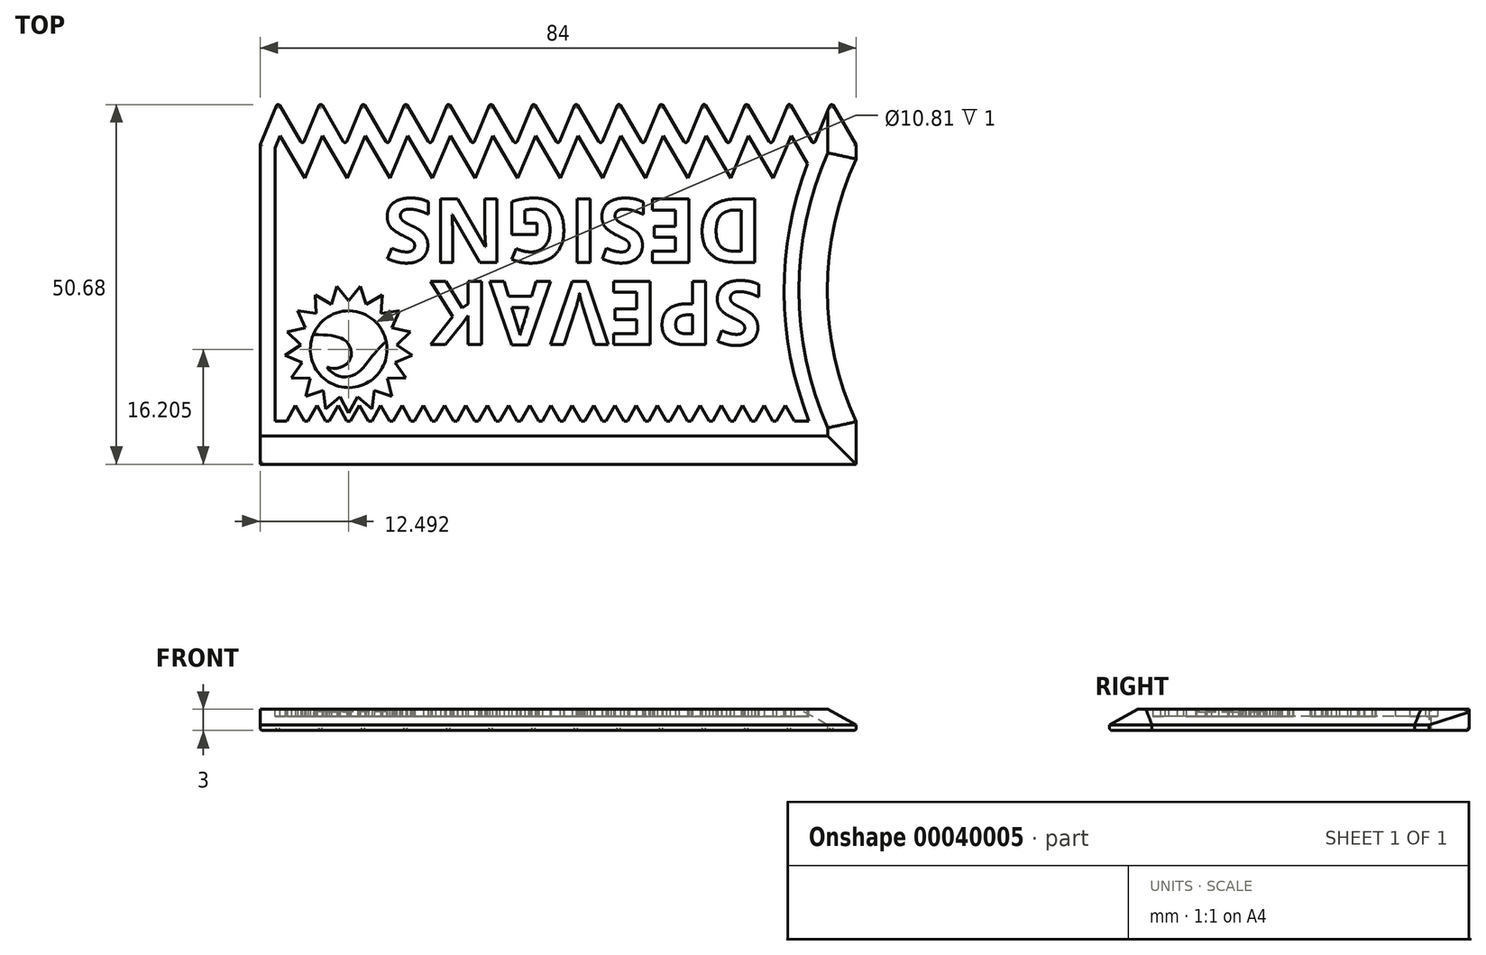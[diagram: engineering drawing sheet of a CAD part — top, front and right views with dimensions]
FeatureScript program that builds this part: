
annotation { "Feature Type Name" : "Feature", "Feature Type Description" : "" }
export const myFeature = defineFeature(function(context is Context, id is Id, definition is map)
    precondition{}
    {
        {
            var Q0;
            Q0=qCreatedBy(makeId("Top.planeOp"),FACE);
            var sketch = newSketch(context, id + "F0", { "sketchPlane" : qUnion([Q0])});
            skLineSegment(sketch, "E0.bottom", {"start": v(0, 0) * mm, "end": v(84, 0) * mm});
            skLineSegment(sketch, "E0.top", {"start": v(2.5, 51) * mm, "end": v(80.5, 51) * mm, "construction": true});
            skLineSegment(sketch, "E0.left", {"start": v(0, 0) * mm, "end": v(0, 45) * mm});
            skLineSegment(sketch, "E0.right", {"start": v(84, 0) * mm, "end": v(84, 45) * mm, "construction": true});
            skLineSegment(sketch, "E1", {"start": v(0, 45) * mm, "end": v(84, 45) * mm, "construction": true});
            skLineSegment(sketch, "E2", {"start": v(0, 45) * mm, "end": v(2.5, 51) * mm});
            skLineSegment(sketch, "E3", {"start": v(2.5, 51) * mm, "end": v(6, 45) * mm});
            skLineSegment(sketch, "E4.1.0.0", {"start": v(6, 45) * mm, "end": v(8.5, 51) * mm});
            skLineSegment(sketch, "E4.1.0.1", {"start": v(8.5, 51) * mm, "end": v(12, 45) * mm});
            skLineSegment(sketch, "E4.2.0.0", {"start": v(12, 45) * mm, "end": v(14.5, 51) * mm});
            skLineSegment(sketch, "E4.2.0.1", {"start": v(14.5, 51) * mm, "end": v(18, 45) * mm});
            skLineSegment(sketch, "E4.3.0.0", {"start": v(18, 45) * mm, "end": v(20.5, 51) * mm});
            skLineSegment(sketch, "E4.3.0.1", {"start": v(20.5, 51) * mm, "end": v(24, 45) * mm});
            skLineSegment(sketch, "E4.4.0.0", {"start": v(24, 45) * mm, "end": v(26.5, 51) * mm});
            skLineSegment(sketch, "E4.4.0.1", {"start": v(26.5, 51) * mm, "end": v(30, 45) * mm});
            skLineSegment(sketch, "E4.5.0.0", {"start": v(30, 45) * mm, "end": v(32.5, 51) * mm});
            skLineSegment(sketch, "E4.5.0.1", {"start": v(32.5, 51) * mm, "end": v(36, 45) * mm});
            skLineSegment(sketch, "E4.6.0.0", {"start": v(36, 45) * mm, "end": v(38.5, 51) * mm});
            skLineSegment(sketch, "E4.6.0.1", {"start": v(38.5, 51) * mm, "end": v(42, 45) * mm});
            skLineSegment(sketch, "E4.7.0.0", {"start": v(42, 45) * mm, "end": v(44.5, 51) * mm});
            skLineSegment(sketch, "E4.7.0.1", {"start": v(44.5, 51) * mm, "end": v(48, 45) * mm});
            skLineSegment(sketch, "E4.8.0.0", {"start": v(48, 45) * mm, "end": v(50.5, 51) * mm});
            skLineSegment(sketch, "E4.8.0.1", {"start": v(50.5, 51) * mm, "end": v(54, 45) * mm});
            skLineSegment(sketch, "E4.9.0.0", {"start": v(54, 45) * mm, "end": v(56.5, 51) * mm});
            skLineSegment(sketch, "E4.9.0.1", {"start": v(56.5, 51) * mm, "end": v(60, 45) * mm});
            skLineSegment(sketch, "E4.10.0.0", {"start": v(60, 45) * mm, "end": v(62.5, 51) * mm});
            skLineSegment(sketch, "E4.10.0.1", {"start": v(62.5, 51) * mm, "end": v(66, 45) * mm});
            skLineSegment(sketch, "E4.11.0.0", {"start": v(66, 45) * mm, "end": v(68.5, 51) * mm});
            skLineSegment(sketch, "E4.11.0.1", {"start": v(68.5, 51) * mm, "end": v(72, 45) * mm});
            skLineSegment(sketch, "E4.12.0.0", {"start": v(72, 45) * mm, "end": v(74.5, 51) * mm});
            skLineSegment(sketch, "E4.12.0.1", {"start": v(74.5, 51) * mm, "end": v(78, 45) * mm});
            skLineSegment(sketch, "E4.13.0.0", {"start": v(78, 45) * mm, "end": v(80.5, 51) * mm});
            skLineSegment(sketch, "E4.13.0.1", {"start": v(80.5, 51) * mm, "end": v(84, 45) * mm});
            skLineSegment(sketch, "E4.direction1", {"start": v(0, 45) * mm, "end": v(6, 45) * mm, "construction": true});
            skLineSegment(sketch, "E5", {"start": v(84, 45) * mm, "end": v(84, 43) * mm});
            skArc(sketch, "E6", {"start": v(84, 43) * mm, "mid": v(79.93, 24.5) * mm, "end": v(84, 6) * mm});
            skLineSegment(sketch, "E7", {"start": v(84, 6) * mm, "end": v(84, 0) * mm});
            skSolve(sketch);
        }
        {
            var Q0;
            Q0=qSketchRegion(id+"F0",true);
            extrude(context, id + "F1", {"entities" : qUnion([Q0]), "depth" : 3 * mm});
        }
        {
            var Q0;
            Q0=makeQuery(id+"F1.opExtrude","CAP_EDGE",EDGE,{"disambiguationData":[OSD([sQuery(id+"F0.wireOp",EDGE,"E5")])],"isStart":false});
            var Q1;
            Q1=makeQuery(id+"F1.opExtrude","CAP_EDGE",EDGE,{"disambiguationData":[OSD([sQuery(id+"F0.wireOp",EDGE,"E6")])],"isStart":false});
            var Q2;
            Q2=makeQuery(id+"F1.opExtrude","CAP_EDGE",EDGE,{"disambiguationData":[OSD([sQuery(id+"F0.wireOp",EDGE,"E0.bottom")])],"isStart":false});
            var Q3;
            Q3=makeQuery(id+"F1.opExtrude","CAP_EDGE",EDGE,{"disambiguationData":[OSD([sQuery(id+"F0.wireOp",EDGE,"E7")])],"isStart":false});
            chamfer(context, id + "F2", {"entities" : qUnion([Q0, Q1, Q2, Q3]), "chamferType" : ChamferType.TWO_OFFSETS, "width1" : 2.2 * mm, "oppositeDirection" : false, "width2" : 4 * mm, "tangentPropagation" : true});
        }
        {
            var Q0;
            Q0=makeQuery(id+"F1.opExtrude","CAP_FACE",FACE,{"disambiguationData":[OSD([sQuery(id+"F0.wireOp",EDGE,"E0.bottom"),sQuery(id+"F0.wireOp",EDGE,"E0.left"),sQuery(id+"F0.wireOp",EDGE,"E2"),sQuery(id+"F0.wireOp",EDGE,"E3"),sQuery(id+"F0.wireOp",EDGE,"E4.1.0.0"),sQuery(id+"F0.wireOp",EDGE,"E4.1.0.1"),sQuery(id+"F0.wireOp",EDGE,"E4.2.0.0"),sQuery(id+"F0.wireOp",EDGE,"E4.2.0.1"),sQuery(id+"F0.wireOp",EDGE,"E4.3.0.0"),sQuery(id+"F0.wireOp",EDGE,"E4.3.0.1"),sQuery(id+"F0.wireOp",EDGE,"E4.4.0.0"),sQuery(id+"F0.wireOp",EDGE,"E4.4.0.1"),sQuery(id+"F0.wireOp",EDGE,"E4.5.0.0"),sQuery(id+"F0.wireOp",EDGE,"E4.5.0.1"),sQuery(id+"F0.wireOp",EDGE,"E4.6.0.0"),sQuery(id+"F0.wireOp",EDGE,"E4.6.0.1"),sQuery(id+"F0.wireOp",EDGE,"E4.7.0.0"),sQuery(id+"F0.wireOp",EDGE,"E4.7.0.1"),sQuery(id+"F0.wireOp",EDGE,"E4.8.0.0"),sQuery(id+"F0.wireOp",EDGE,"E4.8.0.1"),sQuery(id+"F0.wireOp",EDGE,"E4.9.0.0"),sQuery(id+"F0.wireOp",EDGE,"E4.9.0.1"),sQuery(id+"F0.wireOp",EDGE,"E4.10.0.0"),sQuery(id+"F0.wireOp",EDGE,"E4.10.0.1"),sQuery(id+"F0.wireOp",EDGE,"E4.11.0.0"),sQuery(id+"F0.wireOp",EDGE,"E4.11.0.1"),sQuery(id+"F0.wireOp",EDGE,"E4.12.0.0"),sQuery(id+"F0.wireOp",EDGE,"E4.12.0.1"),sQuery(id+"F0.wireOp",EDGE,"E4.13.0.0"),sQuery(id+"F0.wireOp",EDGE,"E4.13.0.1"),sQuery(id+"F0.wireOp",EDGE,"E5"),sQuery(id+"F0.wireOp",EDGE,"E6"),sQuery(id+"F0.wireOp",EDGE,"E7")])],"isStart":false});
            var sketch = newSketch(context, id + "F3", { "sketchPlane" : qUnion([Q0])});
            skLineSegment(sketch, "E8.0", {"start": v(2.1, 44.58) * mm, "end": v(2.1, 6.1) * mm});
            skLineSegment(sketch, "E8.1", {"start": v(2.81, 46.3) * mm, "end": v(2.1, 44.58) * mm});
            skLineSegment(sketch, "E8.2", {"start": v(6.31, 40.3) * mm, "end": v(2.81, 46.3) * mm});
            skLineSegment(sketch, "E8.3", {"start": v(8.81, 46.3) * mm, "end": v(6.31, 40.3) * mm});
            skLineSegment(sketch, "E8.4", {"start": v(12.31, 40.3) * mm, "end": v(8.81, 46.3) * mm});
            skLineSegment(sketch, "E8.5", {"start": v(14.81, 46.3) * mm, "end": v(12.31, 40.3) * mm});
            skLineSegment(sketch, "E8.6", {"start": v(18.31, 40.3) * mm, "end": v(14.81, 46.3) * mm});
            skLineSegment(sketch, "E8.7", {"start": v(2.1, 6.1) * mm, "end": v(77.32, 6.1) * mm});
            skArc(sketch, "E8.8", {"start": v(77.32, 6.1) * mm, "mid": v(73.83, 24.2) * mm, "end": v(77.11, 42.35) * mm});
            skLineSegment(sketch, "E8.9", {"start": v(77.11, 42.35) * mm, "end": v(74.81, 46.3) * mm});
            skLineSegment(sketch, "E8.10", {"start": v(74.81, 46.3) * mm, "end": v(72.31, 40.3) * mm});
            skLineSegment(sketch, "E8.11", {"start": v(72.31, 40.3) * mm, "end": v(68.81, 46.3) * mm});
            skLineSegment(sketch, "E8.12", {"start": v(68.81, 46.3) * mm, "end": v(66.31, 40.3) * mm});
            skLineSegment(sketch, "E8.13", {"start": v(66.31, 40.3) * mm, "end": v(62.81, 46.3) * mm});
            skLineSegment(sketch, "E8.14", {"start": v(62.81, 46.3) * mm, "end": v(60.31, 40.3) * mm});
            skLineSegment(sketch, "E8.15", {"start": v(60.31, 40.3) * mm, "end": v(56.81, 46.3) * mm});
            skLineSegment(sketch, "E8.16", {"start": v(56.81, 46.3) * mm, "end": v(54.31, 40.3) * mm});
            skLineSegment(sketch, "E8.17", {"start": v(54.31, 40.3) * mm, "end": v(50.81, 46.3) * mm});
            skLineSegment(sketch, "E8.18", {"start": v(50.81, 46.3) * mm, "end": v(48.31, 40.3) * mm});
            skLineSegment(sketch, "E8.19", {"start": v(48.31, 40.3) * mm, "end": v(44.81, 46.3) * mm});
            skLineSegment(sketch, "E8.20", {"start": v(44.81, 46.3) * mm, "end": v(42.31, 40.3) * mm});
            skLineSegment(sketch, "E8.21", {"start": v(42.31, 40.3) * mm, "end": v(38.81, 46.3) * mm});
            skLineSegment(sketch, "E8.22", {"start": v(38.81, 46.3) * mm, "end": v(36.31, 40.3) * mm});
            skLineSegment(sketch, "E8.23", {"start": v(36.31, 40.3) * mm, "end": v(32.81, 46.3) * mm});
            skLineSegment(sketch, "E8.24", {"start": v(32.81, 46.3) * mm, "end": v(30.31, 40.3) * mm});
            skLineSegment(sketch, "E8.25", {"start": v(30.31, 40.3) * mm, "end": v(26.81, 46.3) * mm});
            skLineSegment(sketch, "E8.26", {"start": v(26.81, 46.3) * mm, "end": v(24.31, 40.3) * mm});
            skLineSegment(sketch, "E8.27", {"start": v(24.31, 40.3) * mm, "end": v(20.81, 46.3) * mm});
            skLineSegment(sketch, "E8.28", {"start": v(20.81, 46.3) * mm, "end": v(18.31, 40.3) * mm});
            skSolve(sketch);
        }
        {
            var Q0;
            Q0=makeQuery(id+"F3.imprint","IMPRINT",FACE,{"disambiguationData":[TD([[makeQuery(id+"F3.imprint","IMPRINT",EDGE,{"derivedFrom":sQuery(id+"F3.wireOp",EDGE,"E8.0")}),1.0]])]});
            extrude(context, id + "F4", {"entities" : qUnion([Q0]), "operationType" : NewBodyOperationType.REMOVE, "oppositeDirection" : true, "depth" : 1 * mm});
        }
        {
            var Q0;
            Q0=makeQuery(id+"F4.boolean.opBoolean","COPY",FACE,{"derivedFrom":makeQuery(id+"F4.opExtrude","CAP_FACE",FACE,{"disambiguationData":[OSD([sQuery(id+"F3.wireOp",EDGE,"E8.0"),sQuery(id+"F3.wireOp",EDGE,"E8.1"),sQuery(id+"F3.wireOp",EDGE,"E8.2"),sQuery(id+"F3.wireOp",EDGE,"E8.3"),sQuery(id+"F3.wireOp",EDGE,"E8.4"),sQuery(id+"F3.wireOp",EDGE,"E8.5"),sQuery(id+"F3.wireOp",EDGE,"E8.6"),sQuery(id+"F3.wireOp",EDGE,"E8.7"),sQuery(id+"F3.wireOp",EDGE,"E8.8"),sQuery(id+"F3.wireOp",EDGE,"E8.9"),sQuery(id+"F3.wireOp",EDGE,"E8.10"),sQuery(id+"F3.wireOp",EDGE,"E8.11"),sQuery(id+"F3.wireOp",EDGE,"E8.12"),sQuery(id+"F3.wireOp",EDGE,"E8.13"),sQuery(id+"F3.wireOp",EDGE,"E8.14"),sQuery(id+"F3.wireOp",EDGE,"E8.15"),sQuery(id+"F3.wireOp",EDGE,"E8.16"),sQuery(id+"F3.wireOp",EDGE,"E8.17"),sQuery(id+"F3.wireOp",EDGE,"E8.18"),sQuery(id+"F3.wireOp",EDGE,"E8.19"),sQuery(id+"F3.wireOp",EDGE,"E8.20"),sQuery(id+"F3.wireOp",EDGE,"E8.21"),sQuery(id+"F3.wireOp",EDGE,"E8.22"),sQuery(id+"F3.wireOp",EDGE,"E8.23"),sQuery(id+"F3.wireOp",EDGE,"E8.24"),sQuery(id+"F3.wireOp",EDGE,"E8.25"),sQuery(id+"F3.wireOp",EDGE,"E8.26"),sQuery(id+"F3.wireOp",EDGE,"E8.27"),sQuery(id+"F3.wireOp",EDGE,"E8.28")])],"isStart":false})});
            var sketch = newSketch(context, id + "F5", { "sketchPlane" : qUnion([Q0])});
            skLineSegment(sketch, "E9", {"start": v(39.71, 6.1) * mm, "end": v(39.71, 40.3) * mm, "construction": true});
            skText(sketch, "E10", { "text": "SPEVAK", "fontName": "OpenSans-Bold.ttf"});
            skText(sketch, "E11", { "text": "DESIGNS", "fontName": "OpenSans-Bold.ttf"});
            skCircle(sketch, "E12", {"center": v(12.5, 16.2) * mm, "radius": 6.8 * mm, "construction": true});
            skCircle(sketch, "E13", {"center": v(12.5, 16.2) * mm, "radius": 9 * mm, "construction": true});
            skLineSegment(sketch, "E14", {"start": v(12.5, 16.2) * mm, "end": v(12.5, 7.2) * mm, "construction": true});
            skLineSegment(sketch, "E15", {"start": v(13.74, 9.52) * mm, "end": v(12.5, 7.2) * mm});
            skLineSegment(sketch, "E16.MirrorCS", {"start": v(11.24, 9.52) * mm, "end": v(12.5, 7.2) * mm});
            skLineSegment(sketch, "E17", {"start": v(12.5, 16.2) * mm, "end": v(13.74, 9.52) * mm, "construction": true});
            skLineSegment(sketch, "E18.1.0", {"start": v(16.07, 10.42) * mm, "end": v(15.74, 7.81) * mm});
            skLineSegment(sketch, "E18.1.1", {"start": v(13.74, 9.52) * mm, "end": v(15.74, 7.81) * mm});
            skLineSegment(sketch, "E18.2.0", {"start": v(17.92, 12.1) * mm, "end": v(18.56, 9.55) * mm});
            skLineSegment(sketch, "E18.2.1", {"start": v(16.07, 10.42) * mm, "end": v(18.56, 9.55) * mm});
            skLineSegment(sketch, "E18.3.0", {"start": v(19.04, 14.34) * mm, "end": v(20.55, 12.2) * mm});
            skLineSegment(sketch, "E18.3.1", {"start": v(17.92, 12.1) * mm, "end": v(20.55, 12.2) * mm});
            skLineSegment(sketch, "E18.4.0", {"start": v(19.27, 16.83) * mm, "end": v(21.45, 15.37) * mm});
            skLineSegment(sketch, "E18.4.1", {"start": v(19.04, 14.34) * mm, "end": v(21.45, 15.37) * mm});
            skLineSegment(sketch, "E18.5.0", {"start": v(18.58, 19.24) * mm, "end": v(21.15, 18.67) * mm});
            skLineSegment(sketch, "E18.5.1", {"start": v(19.27, 16.83) * mm, "end": v(21.15, 18.67) * mm});
            skLineSegment(sketch, "E18.6.0", {"start": v(17.08, 21.23) * mm, "end": v(19.67, 21.63) * mm});
            skLineSegment(sketch, "E18.6.1", {"start": v(18.58, 19.24) * mm, "end": v(19.67, 21.63) * mm});
            skLineSegment(sketch, "E18.7.0", {"start": v(14.95, 22.55) * mm, "end": v(17.23, 23.86) * mm});
            skLineSegment(sketch, "E18.7.1", {"start": v(17.08, 21.23) * mm, "end": v(17.23, 23.86) * mm});
            skLineSegment(sketch, "E18.8.0", {"start": v(12.5, 23) * mm, "end": v(14.15, 25.05) * mm});
            skLineSegment(sketch, "E18.8.1", {"start": v(14.95, 22.55) * mm, "end": v(14.15, 25.05) * mm});
            skLineSegment(sketch, "E18.9.0", {"start": v(10.03, 22.55) * mm, "end": v(10.84, 25.05) * mm});
            skLineSegment(sketch, "E18.9.1", {"start": v(12.5, 23) * mm, "end": v(10.84, 25.05) * mm});
            skLineSegment(sketch, "E18.10.0", {"start": v(7.9, 21.23) * mm, "end": v(7.75, 23.86) * mm});
            skLineSegment(sketch, "E18.10.1", {"start": v(10.03, 22.55) * mm, "end": v(7.75, 23.86) * mm});
            skLineSegment(sketch, "E18.11.0", {"start": v(6.4, 19.24) * mm, "end": v(5.3, 21.63) * mm});
            skLineSegment(sketch, "E18.11.1", {"start": v(7.9, 21.23) * mm, "end": v(5.3, 21.63) * mm});
            skLineSegment(sketch, "E18.12.0", {"start": v(5.72, 16.83) * mm, "end": v(3.84, 18.67) * mm});
            skLineSegment(sketch, "E18.12.1", {"start": v(6.4, 19.24) * mm, "end": v(3.84, 18.67) * mm});
            skLineSegment(sketch, "E18.13.0", {"start": v(5.95, 14.34) * mm, "end": v(3.53, 15.37) * mm});
            skLineSegment(sketch, "E18.13.1", {"start": v(5.72, 16.83) * mm, "end": v(3.53, 15.37) * mm});
            skLineSegment(sketch, "E18.14.0", {"start": v(7.06, 12.1) * mm, "end": v(4.44, 12.2) * mm});
            skLineSegment(sketch, "E18.14.1", {"start": v(5.95, 14.34) * mm, "end": v(4.44, 12.2) * mm});
            skLineSegment(sketch, "E18.15.0", {"start": v(8.91, 10.42) * mm, "end": v(6.43, 9.55) * mm});
            skLineSegment(sketch, "E18.15.1", {"start": v(7.06, 12.1) * mm, "end": v(6.43, 9.55) * mm});
            skLineSegment(sketch, "E18.16.0", {"start": v(11.24, 9.52) * mm, "end": v(9.24, 7.81) * mm});
            skLineSegment(sketch, "E18.16.1", {"start": v(8.91, 10.42) * mm, "end": v(9.24, 7.81) * mm});
            skCircle(sketch, "E19", {"center": v(12.5, 16.2) * mm, "radius": 5.4 * mm});
            skLineSegment(sketch, "E20", {"start": v(3.75, 6.1) * mm, "end": v(5, 8.3) * mm});
            skLineSegment(sketch, "E21", {"start": v(5, 8.3) * mm, "end": v(6.25, 6.1) * mm});
            skLineSegment(sketch, "E22", {"start": v(6.25, 6.1) * mm, "end": v(3.75, 6.1) * mm, "construction": true});
            skLineSegment(sketch, "E23", {"start": v(5, 6.1) * mm, "end": v(5, 9.23) * mm, "construction": true});
            skLineSegment(sketch, "E24", {"start": v(3.75, 6.1) * mm, "end": v(6.25, 6.1) * mm});
            skLineSegment(sketch, "E25", {"start": v(6.25, 6.1) * mm, "end": v(3.75, 6.1) * mm});
            skLineSegment(sketch, "E26.1.0.0", {"start": v(6.75, 6.1) * mm, "end": v(9.25, 6.1) * mm});
            skLineSegment(sketch, "E26.1.0.1", {"start": v(6.75, 6.1) * mm, "end": v(8, 8.3) * mm});
            skLineSegment(sketch, "E26.1.0.2", {"start": v(8, 8.3) * mm, "end": v(9.25, 6.1) * mm});
            skLineSegment(sketch, "E26.2.0.0", {"start": v(9.75, 6.1) * mm, "end": v(12.25, 6.1) * mm});
            skLineSegment(sketch, "E26.2.0.1", {"start": v(9.75, 6.1) * mm, "end": v(11, 8.3) * mm});
            skLineSegment(sketch, "E26.2.0.2", {"start": v(11, 8.3) * mm, "end": v(12.25, 6.1) * mm});
            skLineSegment(sketch, "E26.3.0.0", {"start": v(12.75, 6.1) * mm, "end": v(15.25, 6.1) * mm});
            skLineSegment(sketch, "E26.3.0.1", {"start": v(12.75, 6.1) * mm, "end": v(14, 8.3) * mm});
            skLineSegment(sketch, "E26.3.0.2", {"start": v(14, 8.3) * mm, "end": v(15.25, 6.1) * mm});
            skLineSegment(sketch, "E26.4.0.0", {"start": v(15.75, 6.1) * mm, "end": v(18.25, 6.1) * mm});
            skLineSegment(sketch, "E26.4.0.1", {"start": v(15.75, 6.1) * mm, "end": v(17, 8.3) * mm});
            skLineSegment(sketch, "E26.4.0.2", {"start": v(17, 8.3) * mm, "end": v(18.25, 6.1) * mm});
            skLineSegment(sketch, "E26.5.0.0", {"start": v(18.75, 6.1) * mm, "end": v(21.25, 6.1) * mm});
            skLineSegment(sketch, "E26.5.0.1", {"start": v(18.75, 6.1) * mm, "end": v(20, 8.3) * mm});
            skLineSegment(sketch, "E26.5.0.2", {"start": v(20, 8.3) * mm, "end": v(21.25, 6.1) * mm});
            skLineSegment(sketch, "E26.6.0.0", {"start": v(21.75, 6.1) * mm, "end": v(24.25, 6.1) * mm});
            skLineSegment(sketch, "E26.6.0.1", {"start": v(21.75, 6.1) * mm, "end": v(23, 8.3) * mm});
            skLineSegment(sketch, "E26.6.0.2", {"start": v(23, 8.3) * mm, "end": v(24.25, 6.1) * mm});
            skLineSegment(sketch, "E26.7.0.0", {"start": v(24.75, 6.1) * mm, "end": v(27.25, 6.1) * mm});
            skLineSegment(sketch, "E26.7.0.1", {"start": v(24.75, 6.1) * mm, "end": v(26, 8.3) * mm});
            skLineSegment(sketch, "E26.7.0.2", {"start": v(26, 8.3) * mm, "end": v(27.25, 6.1) * mm});
            skLineSegment(sketch, "E26.8.0.0", {"start": v(27.75, 6.1) * mm, "end": v(30.25, 6.1) * mm});
            skLineSegment(sketch, "E26.8.0.1", {"start": v(27.75, 6.1) * mm, "end": v(29, 8.3) * mm});
            skLineSegment(sketch, "E26.8.0.2", {"start": v(29, 8.3) * mm, "end": v(30.25, 6.1) * mm});
            skLineSegment(sketch, "E26.9.0.0", {"start": v(30.75, 6.1) * mm, "end": v(33.25, 6.1) * mm});
            skLineSegment(sketch, "E26.9.0.1", {"start": v(30.75, 6.1) * mm, "end": v(32, 8.3) * mm});
            skLineSegment(sketch, "E26.9.0.2", {"start": v(32, 8.3) * mm, "end": v(33.25, 6.1) * mm});
            skLineSegment(sketch, "E26.10.0.0", {"start": v(33.75, 6.1) * mm, "end": v(36.25, 6.1) * mm});
            skLineSegment(sketch, "E26.10.0.1", {"start": v(33.75, 6.1) * mm, "end": v(35, 8.3) * mm});
            skLineSegment(sketch, "E26.10.0.2", {"start": v(35, 8.3) * mm, "end": v(36.25, 6.1) * mm});
            skLineSegment(sketch, "E26.11.0.0", {"start": v(36.75, 6.1) * mm, "end": v(39.25, 6.1) * mm});
            skLineSegment(sketch, "E26.11.0.1", {"start": v(36.75, 6.1) * mm, "end": v(38, 8.3) * mm});
            skLineSegment(sketch, "E26.11.0.2", {"start": v(38, 8.3) * mm, "end": v(39.25, 6.1) * mm});
            skLineSegment(sketch, "E26.12.0.0", {"start": v(39.75, 6.1) * mm, "end": v(42.25, 6.1) * mm});
            skLineSegment(sketch, "E26.12.0.1", {"start": v(39.75, 6.1) * mm, "end": v(41, 8.3) * mm});
            skLineSegment(sketch, "E26.12.0.2", {"start": v(41, 8.3) * mm, "end": v(42.25, 6.1) * mm});
            skLineSegment(sketch, "E26.13.0.0", {"start": v(42.75, 6.1) * mm, "end": v(45.25, 6.1) * mm});
            skLineSegment(sketch, "E26.13.0.1", {"start": v(42.75, 6.1) * mm, "end": v(44, 8.3) * mm});
            skLineSegment(sketch, "E26.13.0.2", {"start": v(44, 8.3) * mm, "end": v(45.25, 6.1) * mm});
            skLineSegment(sketch, "E26.14.0.0", {"start": v(45.75, 6.1) * mm, "end": v(48.25, 6.1) * mm});
            skLineSegment(sketch, "E26.14.0.1", {"start": v(45.75, 6.1) * mm, "end": v(47, 8.3) * mm});
            skLineSegment(sketch, "E26.14.0.2", {"start": v(47, 8.3) * mm, "end": v(48.25, 6.1) * mm});
            skLineSegment(sketch, "E26.15.0.0", {"start": v(48.75, 6.1) * mm, "end": v(51.25, 6.1) * mm});
            skLineSegment(sketch, "E26.15.0.1", {"start": v(48.75, 6.1) * mm, "end": v(50, 8.3) * mm});
            skLineSegment(sketch, "E26.15.0.2", {"start": v(50, 8.3) * mm, "end": v(51.25, 6.1) * mm});
            skLineSegment(sketch, "E26.16.0.0", {"start": v(51.75, 6.1) * mm, "end": v(54.25, 6.1) * mm});
            skLineSegment(sketch, "E26.16.0.1", {"start": v(51.75, 6.1) * mm, "end": v(53, 8.3) * mm});
            skLineSegment(sketch, "E26.16.0.2", {"start": v(53, 8.3) * mm, "end": v(54.25, 6.1) * mm});
            skLineSegment(sketch, "E26.17.0.0", {"start": v(54.75, 6.1) * mm, "end": v(57.25, 6.1) * mm});
            skLineSegment(sketch, "E26.17.0.1", {"start": v(54.75, 6.1) * mm, "end": v(56, 8.3) * mm});
            skLineSegment(sketch, "E26.17.0.2", {"start": v(56, 8.3) * mm, "end": v(57.25, 6.1) * mm});
            skLineSegment(sketch, "E26.18.0.0", {"start": v(57.75, 6.1) * mm, "end": v(60.25, 6.1) * mm});
            skLineSegment(sketch, "E26.18.0.1", {"start": v(57.75, 6.1) * mm, "end": v(59, 8.3) * mm});
            skLineSegment(sketch, "E26.18.0.2", {"start": v(59, 8.3) * mm, "end": v(60.25, 6.1) * mm});
            skLineSegment(sketch, "E26.19.0.0", {"start": v(60.75, 6.1) * mm, "end": v(63.25, 6.1) * mm});
            skLineSegment(sketch, "E26.19.0.1", {"start": v(60.75, 6.1) * mm, "end": v(62, 8.3) * mm});
            skLineSegment(sketch, "E26.19.0.2", {"start": v(62, 8.3) * mm, "end": v(63.25, 6.1) * mm});
            skLineSegment(sketch, "E26.20.0.0", {"start": v(63.75, 6.1) * mm, "end": v(66.25, 6.1) * mm});
            skLineSegment(sketch, "E26.20.0.1", {"start": v(63.75, 6.1) * mm, "end": v(65, 8.3) * mm});
            skLineSegment(sketch, "E26.20.0.2", {"start": v(65, 8.3) * mm, "end": v(66.25, 6.1) * mm});
            skLineSegment(sketch, "E26.21.0.0", {"start": v(66.75, 6.1) * mm, "end": v(69.25, 6.1) * mm});
            skLineSegment(sketch, "E26.21.0.1", {"start": v(66.75, 6.1) * mm, "end": v(68, 8.3) * mm});
            skLineSegment(sketch, "E26.21.0.2", {"start": v(68, 8.3) * mm, "end": v(69.25, 6.1) * mm});
            skLineSegment(sketch, "E26.22.0.0", {"start": v(69.75, 6.1) * mm, "end": v(72.25, 6.1) * mm});
            skLineSegment(sketch, "E26.22.0.1", {"start": v(69.75, 6.1) * mm, "end": v(71, 8.3) * mm});
            skLineSegment(sketch, "E26.22.0.2", {"start": v(71, 8.3) * mm, "end": v(72.25, 6.1) * mm});
            skLineSegment(sketch, "E26.direction1", {"start": v(3.75, 6.1) * mm, "end": v(6.75, 6.1) * mm, "construction": true});
            skLineSegment(sketch, "E27.0.23.0", {"start": v(72.75, 6.1) * mm, "end": v(75.25, 6.1) * mm});
            skLineSegment(sketch, "E27.3.23.0", {"start": v(72.75, 6.1) * mm, "end": v(74, 8.3) * mm});
            skLineSegment(sketch, "E27.6.23.0", {"start": v(74, 8.3) * mm, "end": v(75.25, 6.1) * mm});
            const initialGuessF5  = {"E10": [0.0708, 0.02577, -1, 0, 0.009], "E11": [0.0708, 0.03738, -1, 0, 0.009]};
            skSetInitialGuess(sketch, initialGuessF5);
            skSolve(sketch);
        }
        {
            var Q0;
            Q0=qSketchRegion(id+"F5",true);
            extrude(context, id + "F6", {"entities" : qUnion([Q0]), "operationType" : NewBodyOperationType.ADD, "depth" : 1 * mm});
        }
        {
            var Q0;
            Q0=makeQuery(id+"F6.boolean.opBoolean","SPLIT",FACE,{"disambiguationData":[TD([makeQuery(id+"F6.opExtrude","SWEPT_FACE",FACE,{"disambiguationData":[OSD([sQuery(id+"F5.wireOp",EDGE,"E19")])]})])],"derivedFrom":makeQuery(id+"F4.boolean.opBoolean","COPY",FACE,{"derivedFrom":makeQuery(id+"F4.opExtrude","CAP_FACE",FACE,{"disambiguationData":[OSD([sQuery(id+"F3.wireOp",EDGE,"E8.0"),sQuery(id+"F3.wireOp",EDGE,"E8.1"),sQuery(id+"F3.wireOp",EDGE,"E8.2"),sQuery(id+"F3.wireOp",EDGE,"E8.3"),sQuery(id+"F3.wireOp",EDGE,"E8.4"),sQuery(id+"F3.wireOp",EDGE,"E8.5"),sQuery(id+"F3.wireOp",EDGE,"E8.6"),sQuery(id+"F3.wireOp",EDGE,"E8.7"),sQuery(id+"F3.wireOp",EDGE,"E8.8"),sQuery(id+"F3.wireOp",EDGE,"E8.9"),sQuery(id+"F3.wireOp",EDGE,"E8.10"),sQuery(id+"F3.wireOp",EDGE,"E8.11"),sQuery(id+"F3.wireOp",EDGE,"E8.12"),sQuery(id+"F3.wireOp",EDGE,"E8.13"),sQuery(id+"F3.wireOp",EDGE,"E8.14"),sQuery(id+"F3.wireOp",EDGE,"E8.15"),sQuery(id+"F3.wireOp",EDGE,"E8.16"),sQuery(id+"F3.wireOp",EDGE,"E8.17"),sQuery(id+"F3.wireOp",EDGE,"E8.18"),sQuery(id+"F3.wireOp",EDGE,"E8.19"),sQuery(id+"F3.wireOp",EDGE,"E8.20"),sQuery(id+"F3.wireOp",EDGE,"E8.21"),sQuery(id+"F3.wireOp",EDGE,"E8.22"),sQuery(id+"F3.wireOp",EDGE,"E8.23"),sQuery(id+"F3.wireOp",EDGE,"E8.24"),sQuery(id+"F3.wireOp",EDGE,"E8.25"),sQuery(id+"F3.wireOp",EDGE,"E8.26"),sQuery(id+"F3.wireOp",EDGE,"E8.27"),sQuery(id+"F3.wireOp",EDGE,"E8.28")])],"isStart":false})})});
            var sketch = newSketch(context, id + "F7", { "sketchPlane" : qUnion([Q0])});
            skFitSpline(sketch, "E28", {"points": [v(17.78, 17.32) * mm, v(15.47, 14.8) * mm, v(13.85, 12.96) * mm, v(11.7, 12.31) * mm, v(9.82, 13.18) * mm, v(9.4, 13.7) * mm], "startDerivative": vector(-10.76, -9.46) * mm, "endDerivative": vector(-3.86, 4.53) * mm});
            skFitSpline(sketch, "E29", {"points": [v(9.4, 13.7) * mm, v(11.54, 13.7) * mm, v(12.82, 15.23) * mm, v(12.35, 17.08) * mm, v(10.9, 17.94) * mm, v(7.49, 18.24) * mm], "startDerivative": vector(8.77, -3.25) * mm, "endDerivative": vector(-17.6, -0.1) * mm});
            skArc(sketch, "E30", {"start": v(17.78, 17.32) * mm, "mid": v(12.98, 21.59) * mm, "end": v(7.49, 18.24) * mm});
            skSolve(sketch);
        }
        {
            var Q0;
            Q0=makeQuery(id+"F7.imprint","IMPRINT",FACE,{"disambiguationData":[TD([[makeQuery(id+"F7.imprint","IMPRINT",EDGE,{"derivedFrom":sQuery(id+"F7.wireOp",EDGE,"E28")}),-1.0]])]});
            extrude(context, id + "F8", {"entities" : qUnion([Q0]), "operationType" : NewBodyOperationType.ADD, "depth" : 0.64 * mm});
        }
        {
            var Q0;
            Q0=makeQuery(id+"F1.opExtrude","SWEPT_EDGE",EDGE,{"disambiguationData":[OSD([sQuery(id+"F0.wireOp",EDGE,"E2"),sQuery(id+"F0.wireOp",EDGE,"E3")])]});
            var Q1;
            Q1=makeQuery(id+"F1.opExtrude","SWEPT_EDGE",EDGE,{"disambiguationData":[OSD([sQuery(id+"F0.wireOp",EDGE,"E4.1.0.0"),sQuery(id+"F0.wireOp",EDGE,"E4.1.0.1")])]});
            var Q2;
            Q2=makeQuery(id+"F1.opExtrude","SWEPT_EDGE",EDGE,{"disambiguationData":[OSD([sQuery(id+"F0.wireOp",EDGE,"E4.2.0.0"),sQuery(id+"F0.wireOp",EDGE,"E4.2.0.1")])]});
            var Q3;
            Q3=makeQuery(id+"F1.opExtrude","SWEPT_EDGE",EDGE,{"disambiguationData":[OSD([sQuery(id+"F0.wireOp",EDGE,"E4.3.0.0"),sQuery(id+"F0.wireOp",EDGE,"E4.3.0.1")])]});
            var Q4;
            Q4=makeQuery(id+"F1.opExtrude","SWEPT_EDGE",EDGE,{"disambiguationData":[OSD([sQuery(id+"F0.wireOp",EDGE,"E4.4.0.0"),sQuery(id+"F0.wireOp",EDGE,"E4.4.0.1")])]});
            var Q5;
            Q5=makeQuery(id+"F1.opExtrude","SWEPT_EDGE",EDGE,{"disambiguationData":[OSD([sQuery(id+"F0.wireOp",EDGE,"E4.5.0.0"),sQuery(id+"F0.wireOp",EDGE,"E4.5.0.1")])]});
            var Q6;
            Q6=makeQuery(id+"F1.opExtrude","SWEPT_EDGE",EDGE,{"disambiguationData":[OSD([sQuery(id+"F0.wireOp",EDGE,"E4.6.0.0"),sQuery(id+"F0.wireOp",EDGE,"E4.6.0.1")])]});
            var Q7;
            Q7=makeQuery(id+"F1.opExtrude","SWEPT_EDGE",EDGE,{"disambiguationData":[OSD([sQuery(id+"F0.wireOp",EDGE,"E4.7.0.0"),sQuery(id+"F0.wireOp",EDGE,"E4.7.0.1")])]});
            var Q8;
            Q8=makeQuery(id+"F1.opExtrude","SWEPT_EDGE",EDGE,{"disambiguationData":[OSD([sQuery(id+"F0.wireOp",EDGE,"E4.8.0.0"),sQuery(id+"F0.wireOp",EDGE,"E4.8.0.1")])]});
            var Q9;
            Q9=makeQuery(id+"F1.opExtrude","SWEPT_EDGE",EDGE,{"disambiguationData":[OSD([sQuery(id+"F0.wireOp",EDGE,"E4.13.0.0"),sQuery(id+"F0.wireOp",EDGE,"E4.13.0.1")])]});
            var Q10;
            Q10=makeQuery(id+"F1.opExtrude","SWEPT_EDGE",EDGE,{"disambiguationData":[OSD([sQuery(id+"F0.wireOp",EDGE,"E4.12.0.0"),sQuery(id+"F0.wireOp",EDGE,"E4.12.0.1")])]});
            var Q11;
            Q11=makeQuery(id+"F1.opExtrude","SWEPT_EDGE",EDGE,{"disambiguationData":[OSD([sQuery(id+"F0.wireOp",EDGE,"E4.11.0.0"),sQuery(id+"F0.wireOp",EDGE,"E4.11.0.1")])]});
            var Q12;
            Q12=makeQuery(id+"F1.opExtrude","SWEPT_EDGE",EDGE,{"disambiguationData":[OSD([sQuery(id+"F0.wireOp",EDGE,"E4.10.0.0"),sQuery(id+"F0.wireOp",EDGE,"E4.10.0.1")])]});
            var Q13;
            Q13=makeQuery(id+"F1.opExtrude","SWEPT_EDGE",EDGE,{"disambiguationData":[OSD([sQuery(id+"F0.wireOp",EDGE,"E4.9.0.0"),sQuery(id+"F0.wireOp",EDGE,"E4.9.0.1")])]});
            var Q14;
            Q14=makeQuery(id+"F1.opExtrude","SWEPT_EDGE",EDGE,{"disambiguationData":[OSD([sQuery(id+"F0.wireOp",EDGE,"E4.12.0.1"),sQuery(id+"F0.wireOp",EDGE,"E4.13.0.0")])]});
            var Q15;
            Q15=makeQuery(id+"F1.opExtrude","SWEPT_EDGE",EDGE,{"disambiguationData":[OSD([sQuery(id+"F0.wireOp",EDGE,"E4.11.0.1"),sQuery(id+"F0.wireOp",EDGE,"E4.12.0.0")])]});
            var Q16;
            Q16=makeQuery(id+"F1.opExtrude","SWEPT_EDGE",EDGE,{"disambiguationData":[OSD([sQuery(id+"F0.wireOp",EDGE,"E4.10.0.1"),sQuery(id+"F0.wireOp",EDGE,"E4.11.0.0")])]});
            var Q17;
            Q17=makeQuery(id+"F1.opExtrude","SWEPT_EDGE",EDGE,{"disambiguationData":[OSD([sQuery(id+"F0.wireOp",EDGE,"E4.9.0.1"),sQuery(id+"F0.wireOp",EDGE,"E4.10.0.0")])]});
            var Q18;
            Q18=makeQuery(id+"F1.opExtrude","SWEPT_EDGE",EDGE,{"disambiguationData":[OSD([sQuery(id+"F0.wireOp",EDGE,"E4.8.0.1"),sQuery(id+"F0.wireOp",EDGE,"E4.9.0.0")])]});
            var Q19;
            Q19=makeQuery(id+"F1.opExtrude","SWEPT_EDGE",EDGE,{"disambiguationData":[OSD([sQuery(id+"F0.wireOp",EDGE,"E4.7.0.1"),sQuery(id+"F0.wireOp",EDGE,"E4.8.0.0")])]});
            var Q20;
            Q20=makeQuery(id+"F1.opExtrude","SWEPT_EDGE",EDGE,{"disambiguationData":[OSD([sQuery(id+"F0.wireOp",EDGE,"E4.6.0.1"),sQuery(id+"F0.wireOp",EDGE,"E4.7.0.0")])]});
            var Q21;
            Q21=makeQuery(id+"F1.opExtrude","SWEPT_EDGE",EDGE,{"disambiguationData":[OSD([sQuery(id+"F0.wireOp",EDGE,"E4.5.0.1"),sQuery(id+"F0.wireOp",EDGE,"E4.6.0.0")])]});
            var Q22;
            Q22=makeQuery(id+"F1.opExtrude","SWEPT_EDGE",EDGE,{"disambiguationData":[OSD([sQuery(id+"F0.wireOp",EDGE,"E4.4.0.1"),sQuery(id+"F0.wireOp",EDGE,"E4.5.0.0")])]});
            var Q23;
            Q23=makeQuery(id+"F1.opExtrude","SWEPT_EDGE",EDGE,{"disambiguationData":[OSD([sQuery(id+"F0.wireOp",EDGE,"E4.3.0.1"),sQuery(id+"F0.wireOp",EDGE,"E4.4.0.0")])]});
            var Q24;
            Q24=makeQuery(id+"F1.opExtrude","SWEPT_EDGE",EDGE,{"disambiguationData":[OSD([sQuery(id+"F0.wireOp",EDGE,"E4.2.0.1"),sQuery(id+"F0.wireOp",EDGE,"E4.3.0.0")])]});
            var Q25;
            Q25=makeQuery(id+"F1.opExtrude","SWEPT_EDGE",EDGE,{"disambiguationData":[OSD([sQuery(id+"F0.wireOp",EDGE,"E4.1.0.1"),sQuery(id+"F0.wireOp",EDGE,"E4.2.0.0")])]});
            var Q26;
            Q26=makeQuery(id+"F1.opExtrude","SWEPT_EDGE",EDGE,{"disambiguationData":[OSD([sQuery(id+"F0.wireOp",EDGE,"E3"),sQuery(id+"F0.wireOp",EDGE,"E4.1.0.0")])]});
            fillet(context, id + "F9", {"entities" : qUnion([Q0, Q1, Q2, Q3, Q4, Q5, Q6, Q7, Q8, Q9, Q10, Q11, Q12, Q13, Q14, Q15, Q16, Q17, Q18, Q19, Q20, Q21, Q22, Q23, Q24, Q25, Q26]), "radius" : 0.25 * mm, "tangentPropagation" : true, "allowEdgeOverflow" : false});
        }
        {
            var Q0;
            Q0=makeQuery(id+"F1.opExtrude","CAP_FACE",FACE,{"disambiguationData":[OSD([sQuery(id+"F0.wireOp",EDGE,"E0.bottom"),sQuery(id+"F0.wireOp",EDGE,"E0.left"),sQuery(id+"F0.wireOp",EDGE,"E2"),sQuery(id+"F0.wireOp",EDGE,"E3"),sQuery(id+"F0.wireOp",EDGE,"E4.1.0.0"),sQuery(id+"F0.wireOp",EDGE,"E4.1.0.1"),sQuery(id+"F0.wireOp",EDGE,"E4.2.0.0"),sQuery(id+"F0.wireOp",EDGE,"E4.2.0.1"),sQuery(id+"F0.wireOp",EDGE,"E4.3.0.0"),sQuery(id+"F0.wireOp",EDGE,"E4.3.0.1"),sQuery(id+"F0.wireOp",EDGE,"E4.4.0.0"),sQuery(id+"F0.wireOp",EDGE,"E4.4.0.1"),sQuery(id+"F0.wireOp",EDGE,"E4.5.0.0"),sQuery(id+"F0.wireOp",EDGE,"E4.5.0.1"),sQuery(id+"F0.wireOp",EDGE,"E4.6.0.0"),sQuery(id+"F0.wireOp",EDGE,"E4.6.0.1"),sQuery(id+"F0.wireOp",EDGE,"E4.7.0.0"),sQuery(id+"F0.wireOp",EDGE,"E4.7.0.1"),sQuery(id+"F0.wireOp",EDGE,"E4.8.0.0"),sQuery(id+"F0.wireOp",EDGE,"E4.8.0.1"),sQuery(id+"F0.wireOp",EDGE,"E4.9.0.0"),sQuery(id+"F0.wireOp",EDGE,"E4.9.0.1"),sQuery(id+"F0.wireOp",EDGE,"E4.10.0.0"),sQuery(id+"F0.wireOp",EDGE,"E4.10.0.1"),sQuery(id+"F0.wireOp",EDGE,"E4.11.0.0"),sQuery(id+"F0.wireOp",EDGE,"E4.11.0.1"),sQuery(id+"F0.wireOp",EDGE,"E4.12.0.0"),sQuery(id+"F0.wireOp",EDGE,"E4.12.0.1"),sQuery(id+"F0.wireOp",EDGE,"E4.13.0.0"),sQuery(id+"F0.wireOp",EDGE,"E4.13.0.1"),sQuery(id+"F0.wireOp",EDGE,"E5"),sQuery(id+"F0.wireOp",EDGE,"E6"),sQuery(id+"F0.wireOp",EDGE,"E7")])],"isStart":true});
            fillet(context, id + "F10", {"entities" : qUnion([Q0]), "radius" : 0.38 * mm, "tangentPropagation" : true, "allowEdgeOverflow" : false});
        }
    });
